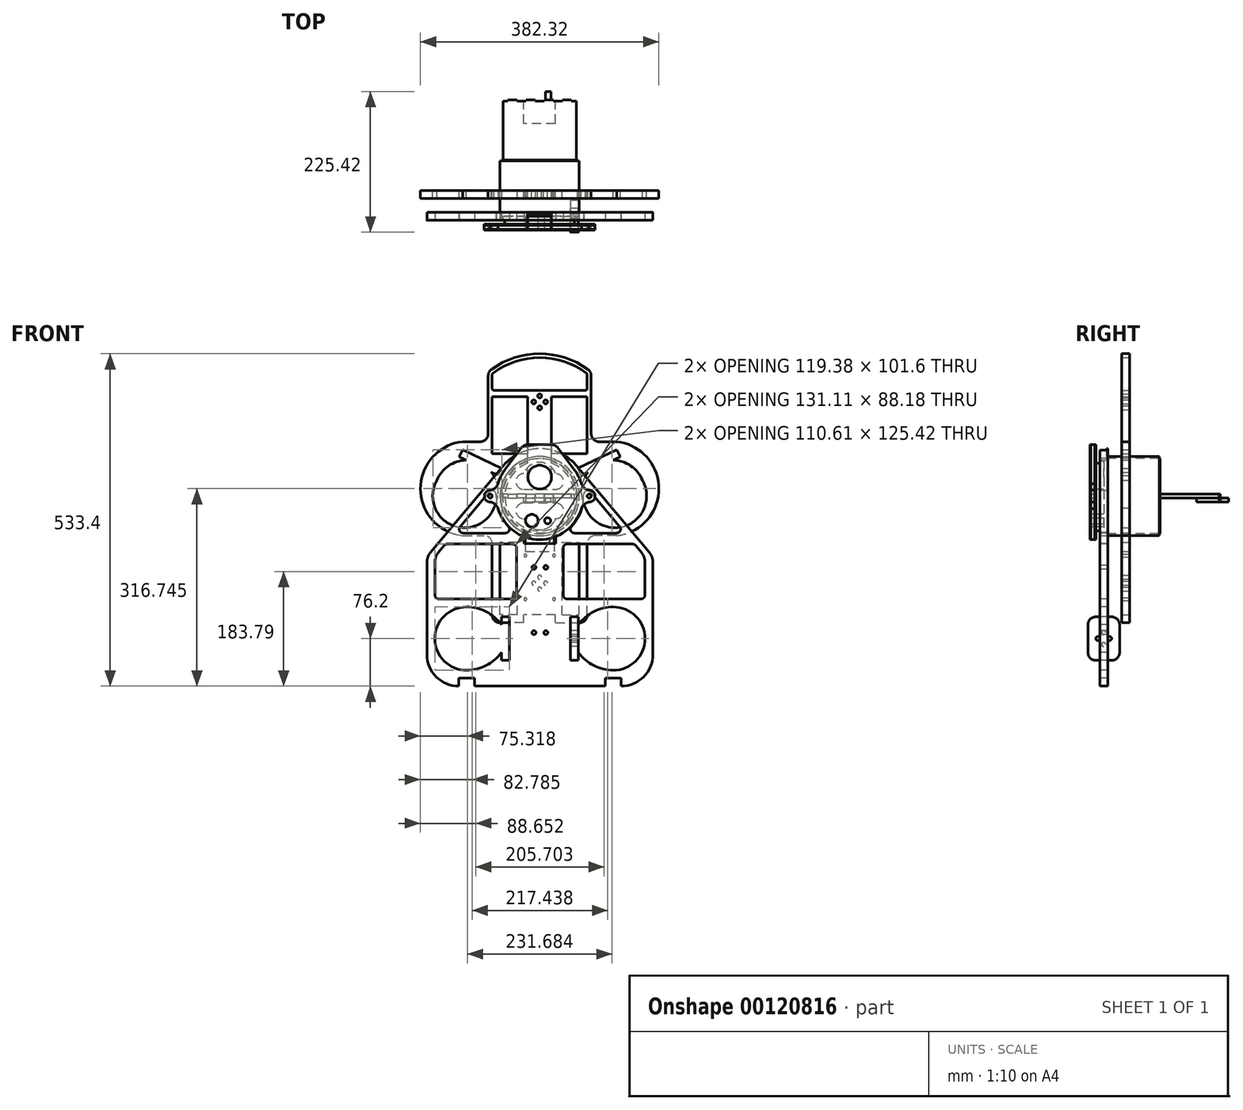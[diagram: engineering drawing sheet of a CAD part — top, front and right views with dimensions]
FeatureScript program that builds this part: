
annotation { "Feature Type Name" : "Feature", "Feature Type Description" : "" }
export const myFeature = defineFeature(function(context is Context, id is Id, definition is map)
    precondition{}
    {
        {
            var Q0;
            Q0=qCreatedBy(makeId("Front.planeOp"),FACE);
            var sketch = newSketch(context, id + "F32", { "sketchPlane" : qUnion([Q0])});
            skCircle(sketch, "E0", {"center": v(0, 0) * mm, "radius": 63.5 * mm});
            skSolve(sketch);
        }
        {
            var Q0;
            Q0=makeQuery(id+"F32.imprint","IMPRINT",FACE,{"disambiguationData":[TD([[makeQuery(id+"F32.imprint","IMPRINT",EDGE,{"derivedFrom":sQuery(id+"F32.wireOp",EDGE,"E0")}),1.0]])]});
            extrude(context, id + "F0", {"entities" : qUnion([Q0]), "endBound" : BoundingType.SYMMETRIC, "depth" : 95.25 * mm});
        }
        {
            var Q0;
            Q0=makeQuery(id+"F0.opExtrude","CAP_FACE",FACE,{"disambiguationData":[OSD([sQuery(id+"F32.wireOp",EDGE,"E0")])],"isStart":false});
            var sketch = newSketch(context, id + "F1", { "sketchPlane" : qUnion([Q0])});
            skPoint(sketch, "E1.middle", {"position": v(0.34, 103.4) * mm});
            skLineSegment(sketch, "E2.right", {"start": v(-180.77, -106.35) * mm, "end": v(-180.77, -254) * mm});
            skLineSegment(sketch, "E3", {"start": v(-174.82, -90.02) * mm, "end": v(-58.18, 48.86) * mm});
            skLineSegment(sketch, "E4", {"start": v(-129.97, -304.8) * mm, "end": v(-129.97, -304.8) * mm});
            skLineSegment(sketch, "E5", {"start": v(0.34, 103.4) * mm, "end": v(0.34, -422.75) * mm, "construction": true});
            skLineSegment(sketch, "E6", {"start": v(-117.27, -177.8) * mm, "end": v(0, -177.8) * mm, "construction": true});
            skLineSegment(sketch, "E7", {"start": v(-117.27, -279.4) * mm, "end": v(0, -279.4) * mm, "construction": true});
            skLineSegment(sketch, "E8.top", {"start": v(-129.97, -292.1) * mm, "end": v(-104.57, -292.1) * mm});
            skLineSegment(sketch, "E8.left", {"start": v(-129.97, -304.8) * mm, "end": v(-129.97, -292.1) * mm});
            skLineSegment(sketch, "E8.right", {"start": v(-104.57, -304.8) * mm, "end": v(-104.57, -292.1) * mm});
            skPoint(sketch, "E8.middle", {"position": v(-117.27, -298.45) * mm});
            skLineSegment(sketch, "E9.trimOffspring", {"start": v(-104.57, -304.8) * mm, "end": v(0.34, -304.8) * mm});
            skLineSegment(sketch, "E10.bottom", {"start": v(0.34, -63.5) * mm, "end": v(0, -63.5) * mm});
            skLineSegment(sketch, "E10.top", {"start": v(25.74, -76.2) * mm, "end": v(-25.06, -76.2) * mm});
            skLineSegment(sketch, "E10.left", {"start": v(25.74, -58.05) * mm, "end": v(25.74, -76.2) * mm});
            skLineSegment(sketch, "E10.right", {"start": v(-25.06, -58.35) * mm, "end": v(-25.06, -76.2) * mm});
            skPoint(sketch, "E10.middle", {"position": v(0.34, -69.85) * mm});
            skArc(sketch, "E11.0", {"start": v(0, -63.5) * mm, "mid": v(0.17, -63.5) * mm, "end": v(0.34, -63.5) * mm});
            skArc(sketch, "E12", {"start": v(-33.6, -53.89) * mm, "mid": v(52.5, 35.7) * mm, "end": v(-62.46, -11.43) * mm});
            skArc(sketch, "E13.trimOffspring", {"start": v(25.74, -58.05) * mm, "mid": v(29.67, 56.14) * mm, "end": v(-62.46, -11.43) * mm});
            skPoint(sketch, "E14.orphan", {"position": v(25.74, -63.5) * mm});
            skPoint(sketch, "E15.orphan", {"position": v(-25.06, -63.5) * mm});
            skCircle(sketch, "E16", {"center": v(-9.18, -114.35) * mm, "radius": 3.18 * mm});
            skCircle(sketch, "E17.MirrorC", {"center": v(9.87, -114.35) * mm, "radius": 3.18 * mm});
            skCircle(sketch, "E18", {"center": v(-9.18, -219.08) * mm, "radius": 3.18 * mm});
            skCircle(sketch, "E19.MirrorC", {"center": v(9.87, -219.08) * mm, "radius": 3.18 * mm});
            skLineSegment(sketch, "E20.bottom", {"start": v(-48.69, -206.38) * mm, "end": v(-61.39, -206.38) * mm, "construction": true});
            skLineSegment(sketch, "E20.top", {"start": v(-48.69, -250.83) * mm, "end": v(-61.39, -250.83) * mm, "construction": true});
            skLineSegment(sketch, "E20.left", {"start": v(-48.69, -206.38) * mm, "end": v(-48.69, -250.83) * mm});
            skLineSegment(sketch, "E20.right", {"start": v(-61.39, -206.38) * mm, "end": v(-61.39, -250.83) * mm, "construction": true});
            skPoint(sketch, "E20.middle", {"position": v(-55.04, -228.6) * mm});
            skLineSegment(sketch, "E21.MirrorCS", {"start": v(49.37, -206.38) * mm, "end": v(49.37, -250.83) * mm});
            skLineSegment(sketch, "E22.MirrorCS", {"start": v(62.07, -206.38) * mm, "end": v(62.07, -250.83) * mm, "construction": true});
            skLineSegment(sketch, "E23", {"start": v(-61.39, -206.38) * mm, "end": v(-61.39, -193.67) * mm});
            skLineSegment(sketch, "E24", {"start": v(-61.39, -193.68) * mm, "end": v(-48.69, -193.68) * mm});
            skLineSegment(sketch, "E25", {"start": v(-48.69, -193.67) * mm, "end": v(-48.69, -206.38) * mm});
            skLineSegment(sketch, "E26", {"start": v(-117.27, -228.6) * mm, "end": v(-55.04, -228.6) * mm, "construction": true});
            skLineSegment(sketch, "E27.MirrorCS", {"start": v(-48.69, -263.53) * mm, "end": v(-48.69, -250.83) * mm});
            skLineSegment(sketch, "E28.MirrorCS", {"start": v(-61.39, -250.83) * mm, "end": v(-61.39, -263.53) * mm});
            skLineSegment(sketch, "E29.MirrorCS", {"start": v(-61.39, -263.53) * mm, "end": v(-48.69, -263.53) * mm});
            skLineSegment(sketch, "E30.MirrorCS", {"start": v(62.07, -206.38) * mm, "end": v(62.07, -193.67) * mm});
            skLineSegment(sketch, "E31.MirrorCS", {"start": v(62.07, -193.68) * mm, "end": v(49.37, -193.68) * mm});
            skLineSegment(sketch, "E32.MirrorCS", {"start": v(49.37, -193.67) * mm, "end": v(49.37, -206.38) * mm});
            skLineSegment(sketch, "E33.MirrorCS", {"start": v(62.07, -250.83) * mm, "end": v(62.07, -263.53) * mm});
            skLineSegment(sketch, "E34.MirrorCS", {"start": v(62.07, -263.53) * mm, "end": v(49.37, -263.53) * mm});
            skLineSegment(sketch, "E35.MirrorCS", {"start": v(49.37, -263.53) * mm, "end": v(49.37, -250.83) * mm});
            skPoint(sketch, "E36.MirrorCS.end.orphan", {"position": v(62.07, -206.38) * mm});
            skPoint(sketch, "E36.MirrorCS.start.orphan", {"position": v(49.37, -206.38) * mm});
            skPoint(sketch, "E37.MirrorCS.end.orphan", {"position": v(62.07, -250.83) * mm});
            skPoint(sketch, "E37.MirrorCS.start.orphan", {"position": v(49.37, -250.83) * mm});
            skLineSegment(sketch, "E38.MirrorCS", {"start": v(105.25, -304.8) * mm, "end": v(0.34, -304.8) * mm});
            skLineSegment(sketch, "E39.MirrorCS", {"start": v(105.25, -304.8) * mm, "end": v(105.25, -292.1) * mm});
            skLineSegment(sketch, "E40.MirrorCS", {"start": v(130.65, -292.1) * mm, "end": v(105.25, -292.1) * mm});
            skLineSegment(sketch, "E41.MirrorCS", {"start": v(130.65, -304.8) * mm, "end": v(130.65, -292.1) * mm});
            skLineSegment(sketch, "E42.MirrorCS", {"start": v(181.45, -97.1) * mm, "end": v(181.45, -254) * mm});
            skLineSegment(sketch, "E43.MirrorCS", {"start": v(181.45, -97.1) * mm, "end": v(58.86, 48.86) * mm});
            skArc(sketch, "E44", {"start": v(58.86, 48.86) * mm, "mid": v(0.34, 76.13) * mm, "end": v(-58.18, 48.86) * mm});
            skPoint(sketch, "E45.visualSharp", {"position": v(-180.77, -304.8) * mm});
            skArc(sketch, "E45.filletArc", {"start": v(-180.77, -254) * mm, "mid": v(-165.89, -289.92) * mm, "end": v(-129.97, -304.8) * mm});
            skArc(sketch, "E46.MirrorCS", {"start": v(181.45, -254) * mm, "mid": v(166.57, -289.92) * mm, "end": v(130.65, -304.8) * mm});
            skPoint(sketch, "E47.MirrorCS.end.orphan", {"position": v(130.65, -304.8) * mm});
            skLineSegment(sketch, "E48", {"start": v(-168.07, -158.75) * mm, "end": v(-168.07, -106.35) * mm});
            skLineSegment(sketch, "E49", {"start": v(-162.12, -90.02) * mm, "end": v(-153.02, -79.19) * mm});
            skArc(sketch, "E50", {"start": v(-62.46, -11.43) * mm, "mid": v(-52.5, -35.7) * mm, "end": v(-33.6, -53.89) * mm});
            skArc(sketch, "E51", {"start": v(-33.6, -53.89) * mm, "mid": v(-29.4, -56.28) * mm, "end": v(-25.06, -58.35) * mm});
            skLineSegment(sketch, "E52", {"start": v(-62.46, -11.43) * mm, "end": v(-62.46, -11.43) * mm});
            skLineSegment(sketch, "E53", {"start": v(-33.6, -53.89) * mm, "end": v(-33.6, -53.89) * mm});
            skArc(sketch, "E54.0", {"start": v(-69.81, 2.25) * mm, "mid": v(-65.18, -25.12) * mm, "end": v(-50.25, -48.52) * mm});
            skLineSegment(sketch, "E55", {"start": v(-36.95, -83.27) * mm, "end": v(-36.95, -158.75) * mm});
            skLineSegment(sketch, "E56", {"start": v(-64.97, 25.65) * mm, "end": v(-64.97, 25.65) * mm});
            skPoint(sketch, "E57.visualSharp", {"position": v(-180.77, -97.1) * mm});
            skArc(sketch, "E57.filletArc", {"start": v(-174.82, -90.02) * mm, "mid": v(-179.23, -97.66) * mm, "end": v(-180.77, -106.35) * mm});
            skPoint(sketch, "E58.visualSharp", {"position": v(-168.07, -97.1) * mm});
            skArc(sketch, "E58.filletArc", {"start": v(-162.12, -90.02) * mm, "mid": v(-166.53, -97.66) * mm, "end": v(-168.07, -106.35) * mm});
            skArc(sketch, "E59.MirrorCS", {"start": v(162.8, -90.02) * mm, "mid": v(167.22, -97.66) * mm, "end": v(168.75, -106.35) * mm});
            skArc(sketch, "E60.MirrorCS", {"start": v(175.5, -90.02) * mm, "mid": v(179.92, -97.66) * mm, "end": v(181.45, -106.35) * mm});
            skLineSegment(sketch, "E61.MirrorCS", {"start": v(128.22, -48.84) * mm, "end": v(81.71, 6.54) * mm});
            skArc(sketch, "E62.MirrorCS", {"start": v(70.5, 2.25) * mm, "mid": v(65.87, -25.12) * mm, "end": v(50.94, -48.52) * mm});
            skLineSegment(sketch, "E63.MirrorCS", {"start": v(37.64, -59.28) * mm, "end": v(37.64, -76.92) * mm, "construction": true});
            skLineSegment(sketch, "E64.MirrorCS", {"start": v(168.75, -158.75) * mm, "end": v(168.75, -106.35) * mm});
            skLineSegment(sketch, "E65", {"start": v(74.77, -201.84) * mm, "end": v(74.77, -201.84) * mm});
            skLineSegment(sketch, "E66.bottom", {"start": v(-54.82, -59.28) * mm, "end": v(-122.67, -59.28) * mm});
            skLineSegment(sketch, "E66.top", {"start": v(-43.3, -76.92) * mm, "end": v(-148.16, -76.92) * mm});
            skLineSegment(sketch, "E66.left", {"start": v(-36.95, -59.28) * mm, "end": v(-36.95, -76.92) * mm, "construction": true});
            skLineSegment(sketch, "E67.MirrorCS", {"start": v(43.99, -76.92) * mm, "end": v(148.84, -76.92) * mm});
            skLineSegment(sketch, "E68.MirrorCS", {"start": v(55.5, -59.28) * mm, "end": v(123.36, -59.28) * mm});
            skArc(sketch, "E69.MirrorCS", {"start": v(117.95, -279.4) * mm, "mid": v(86.57, -271.84) * mm, "end": v(62.07, -250.83) * mm});
            skArc(sketch, "E70.MirrorCS", {"start": v(168.75, -228.6) * mm, "mid": v(153.87, -264.52) * mm, "end": v(117.95, -279.4) * mm});
            skArc(sketch, "E71", {"start": v(-117.27, -279.4) * mm, "mid": v(-85.88, -271.84) * mm, "end": v(-61.39, -250.83) * mm});
            skArc(sketch, "E72", {"start": v(-168.07, -228.6) * mm, "mid": v(-153.19, -264.52) * mm, "end": v(-117.27, -279.4) * mm});
            skArc(sketch, "E73.MirrorCS", {"start": v(-117.27, -177.8) * mm, "mid": v(-85.88, -185.36) * mm, "end": v(-61.39, -206.38) * mm});
            skArc(sketch, "E74.MirrorCS", {"start": v(-168.07, -228.6) * mm, "mid": v(-153.19, -192.68) * mm, "end": v(-117.27, -177.8) * mm});
            skLineSegment(sketch, "E75", {"start": v(-43.3, -165.1) * mm, "end": v(-161.72, -165.1) * mm});
            skArc(sketch, "E76.MirrorCS", {"start": v(117.95, -177.8) * mm, "mid": v(86.57, -185.36) * mm, "end": v(62.07, -206.38) * mm});
            skArc(sketch, "E77.MirrorCS", {"start": v(168.75, -228.6) * mm, "mid": v(153.87, -192.68) * mm, "end": v(117.95, -177.8) * mm});
            skLineSegment(sketch, "E78.MirrorCS", {"start": v(43.99, -165.1) * mm, "end": v(162.4, -165.1) * mm});
            skLineSegment(sketch, "E79", {"start": v(37.64, -83.27) * mm, "end": v(37.64, -158.75) * mm});
            skLineSegment(sketch, "E80", {"start": v(-36.95, -76.92) * mm, "end": v(-36.95, -76.92) * mm});
            skPoint(sketch, "E81.visualSharp", {"position": v(-36.95, -165.1) * mm});
            skArc(sketch, "E81.filletArc", {"start": v(-43.3, -165.1) * mm, "mid": v(-38.81, -163.24) * mm, "end": v(-36.95, -158.75) * mm});
            skPoint(sketch, "E82.newPointA", {"position": v(-168.07, -165.1) * mm});
            skPoint(sketch, "E82.newPointB", {"position": v(-168.07, -163.76) * mm});
            skArc(sketch, "E82.filletArc", {"start": v(-168.07, -158.75) * mm, "mid": v(-166.2, -163.24) * mm, "end": v(-161.72, -165.1) * mm});
            skPoint(sketch, "E83.newPointA", {"position": v(-36.95, -59.28) * mm});
            skPoint(sketch, "E83.newPointB", {"position": v(-36.95, -76.92) * mm});
            skArc(sketch, "E83.filletArc", {"start": v(-36.95, -83.27) * mm, "mid": v(-38.81, -78.78) * mm, "end": v(-43.3, -76.92) * mm});
            skPoint(sketch, "E84.visualSharp", {"position": v(37.64, -76.92) * mm});
            skArc(sketch, "E84.filletArc", {"start": v(43.99, -76.92) * mm, "mid": v(39.5, -78.78) * mm, "end": v(37.64, -83.27) * mm});
            skPoint(sketch, "E85.newPointA", {"position": v(-64.97, 25.65) * mm});
            skPoint(sketch, "E85.newPointB", {"position": v(-151.11, -76.92) * mm});
            skArc(sketch, "E85.filletArc", {"start": v(-148.16, -76.92) * mm, "mid": v(-150.84, -77.51) * mm, "end": v(-153.02, -79.19) * mm});
            skLineSegment(sketch, "E86", {"start": v(-81.02, 6.54) * mm, "end": v(-127.53, -48.84) * mm});
            skPoint(sketch, "E87.visualSharp", {"position": v(-136.3, -59.28) * mm});
            skArc(sketch, "E87.filletArc", {"start": v(-127.53, -48.84) * mm, "mid": v(-128.43, -55.6) * mm, "end": v(-122.67, -59.28) * mm});
            skArc(sketch, "E88.filletArc", {"start": v(-69.81, 2.25) * mm, "mid": v(-73.9, 8.38) * mm, "end": v(-81.02, 6.54) * mm});
            skArc(sketch, "E89.filletArc", {"start": v(-54.82, -59.28) * mm, "mid": v(-48.97, -55.4) * mm, "end": v(-50.25, -48.52) * mm});
            skPoint(sketch, "E90.visualSharp", {"position": v(37.64, -59.28) * mm});
            skArc(sketch, "E90.filletArc", {"start": v(50.94, -48.52) * mm, "mid": v(49.66, -55.4) * mm, "end": v(55.5, -59.28) * mm});
            skPoint(sketch, "E91.visualSharp", {"position": v(65.66, 25.65) * mm});
            skArc(sketch, "E91.filletArc", {"start": v(81.71, 6.54) * mm, "mid": v(74.58, 8.38) * mm, "end": v(70.5, 2.25) * mm});
            skPoint(sketch, "E92.newPointA", {"position": v(162.8, -90.02) * mm});
            skPoint(sketch, "E92.newPointB", {"position": v(136.98, -59.28) * mm});
            skArc(sketch, "E92.filletArc", {"start": v(123.36, -59.28) * mm, "mid": v(129.11, -55.6) * mm, "end": v(128.22, -48.84) * mm});
            skLineSegment(sketch, "E93", {"start": v(162.8, -90.02) * mm, "end": v(153.7, -79.19) * mm});
            skPoint(sketch, "E94.visualSharp", {"position": v(151.8, -76.92) * mm});
            skArc(sketch, "E94.filletArc", {"start": v(153.7, -79.19) * mm, "mid": v(151.53, -77.51) * mm, "end": v(148.84, -76.92) * mm});
            skPoint(sketch, "E95.newPointA", {"position": v(168.75, -163.76) * mm});
            skPoint(sketch, "E95.newPointB", {"position": v(168.75, -165.1) * mm});
            skArc(sketch, "E95.filletArc", {"start": v(162.4, -165.1) * mm, "mid": v(166.9, -163.24) * mm, "end": v(168.75, -158.75) * mm});
            skPoint(sketch, "E96.visualSharp", {"position": v(37.64, -165.1) * mm});
            skArc(sketch, "E96.filletArc", {"start": v(37.64, -158.75) * mm, "mid": v(39.5, -163.24) * mm, "end": v(43.99, -165.1) * mm});
            skSolve(sketch);
        }
        {
            var Q0;
            Q0=makeQuery(id+"F1.imprint","IMPRINT",FACE,{"disambiguationData":[TD([[makeQuery(id+"F1.imprint","IMPRINT",EDGE,{"derivedFrom":sQuery(id+"F1.wireOp",EDGE,"E2.left")}),-1.0]])]});
            var Q1;
            Q1=makeQuery(id+"F1.imprint","IMPRINT",FACE,{"disambiguationData":[TD([[makeQuery(id+"F1.imprint","IMPRINT",EDGE,{"derivedFrom":makeQuery(id+"F0.opExtrude","CAP_EDGE",EDGE,{"disambiguationData":[OSD([sQuery(id+"F32.wireOp",EDGE,"E0")])],"isStart":false})}),-1.0]])]});
            var Q2;
            {var subQ0=sQuery(id+"F1.wireOp",EDGE,"E10.left");Q2=makeQuery(id+"F1.imprint","IMPRINT",FACE,{"disambiguationData":[TD([[makeQuery(id+"F1.imprint","IMPRINT",EDGE,{"derivedFrom":subQ0}),1.0]])]});}
            var Q3;
            Q3=makeQuery(id+"F1.imprint","IMPRINT",FACE,{"disambiguationData":[TD([[makeQuery(id+"F1.imprint","IMPRINT",EDGE,{"derivedFrom":sQuery(id+"F1.wireOp",EDGE,"E2.right")}),1.0]])]});
            var Q4;
            {var subQ0=sQuery(id+"F1.wireOp",EDGE,"E66.bottom");Q4=makeQuery(id+"F1.imprint","IMPRINT",FACE,{"disambiguationData":[TD([[makeQuery(id+"F1.imprint","IMPRINT",EDGE,{"derivedFrom":subQ0}),1.0]])]});}
            var Q5;
            {var subQ0=sQuery(id+"F1.wireOp",EDGE,"E67.MirrorCS");Q5=makeQuery(id+"F1.imprint","IMPRINT",FACE,{"disambiguationData":[TD([[makeQuery(id+"F1.imprint","IMPRINT",EDGE,{"derivedFrom":subQ0}),1.0]])]});}
            extrude(context, id + "F2", {"entities" : qUnion([Q0, Q1, Q2, Q3, Q4, Q5]), "oppositeDirection" : true, "depth" : 12.7 * mm});
        }
        {
            var Q0;
            Q0=makeQuery(id+"F0.opExtrude","CAP_FACE",FACE,{"disambiguationData":[OSD([sQuery(id+"F32.wireOp",EDGE,"E0")])],"isStart":false});
            var sketch = newSketch(context, id + "F3", { "sketchPlane" : qUnion([Q0])});
            skCircle(sketch, "E97", {"center": v(0, 0) * mm, "radius": 60.2 * mm});
            skSolve(sketch);
        }
        {
            var Q0;
            Q0=makeQuery(id+"F3.imprint","IMPRINT",FACE,{"disambiguationData":[TD([[makeQuery(id+"F3.imprint","IMPRINT",EDGE,{"derivedFrom":sQuery(id+"F3.wireOp",EDGE,"E97")}),1.0]])]});
            extrude(context, id + "F4", {"entities" : qUnion([Q0]), "operationType" : NewBodyOperationType.REMOVE, "endBound" : BoundingType.THROUGH_ALL, "oppositeDirection" : true, "depth" : 25.4 * mm});
        }
        {
            var Q0;
            Q0=makeQuery(id+"F0.opExtrude","CAP_FACE",FACE,{"disambiguationData":[OSD([sQuery(id+"F32.wireOp",EDGE,"E0")])],"isStart":false});
            var sketch = newSketch(context, id + "F5", { "sketchPlane" : qUnion([Q0])});
            skCircle(sketch, "E98", {"center": v(0, 0) * mm, "radius": 59.2 * mm});
            skSolve(sketch);
        }
        {
            var Q0;
            Q0=makeQuery(id+"F5.imprint","IMPRINT",FACE,{"disambiguationData":[TD([[makeQuery(id+"F5.imprint","IMPRINT",EDGE,{"derivedFrom":sQuery(id+"F5.wireOp",EDGE,"E98")}),1.0]])]});
            extrude(context, id + "F6", {"entities" : qUnion([Q0]), "oppositeDirection" : true, "depth" : 6.35 * mm});
        }
        {
            var Q0;
            Q0=makeQuery(id+"F6.opExtrude","CAP_FACE",FACE,{"disambiguationData":[OSD([sQuery(id+"F5.wireOp",EDGE,"E98")])],"isStart":true});
            var sketch = newSketch(context, id + "F7", { "sketchPlane" : qUnion([Q0])});
            skCircle(sketch, "E99", {"center": v(0, 0) * mm, "radius": 55.88 * mm});
            skSolve(sketch);
        }
        {
            var Q0;
            Q0 = qSketchRegion(id + "F7", true);
            extrude(context, id + "F8", {"entities" : qUnion([Q0]), "depth" : 6.35 * mm});
        }
        {
            var Q0;
            Q0=makeQuery(id+"F8.opExtrude","CAP_FACE",FACE,{"disambiguationData":[OSD([sQuery(id+"F7.wireOp",EDGE,"E99")])],"isStart":false});
            var sketch = newSketch(context, id + "F9", { "sketchPlane" : qUnion([Q0])});
            skArc(sketch, "E100", {"start": v(66.89, 20) * mm, "mid": v(0, 69.81) * mm, "end": v(-66.89, 20) * mm});
            skCircle(sketch, "E101", {"center": v(-79.34, 0) * mm, "radius": 3.18 * mm});
            skArc(sketch, "E102.0", {"start": v(-79.34, 9.52) * mm, "mid": v(-88.86, 0) * mm, "end": v(-79.34, -9.52) * mm});
            skLineSegment(sketch, "E103", {"start": v(-79.4, 9.53) * mm, "end": v(-79.34, 9.53) * mm});
            skArc(sketch, "E104", {"start": v(-79.34, 9.53) * mm, "mid": v(-71.62, 13) * mm, "end": v(-66.89, 20) * mm});
            skArc(sketch, "E105.MirrorCS", {"start": v(-79.34, -9.53) * mm, "mid": v(-71.62, -13) * mm, "end": v(-66.89, -20) * mm});
            skArc(sketch, "E106.MirrorCS", {"start": v(79.34, 9.53) * mm, "mid": v(71.62, 13) * mm, "end": v(66.89, 20) * mm});
            skArc(sketch, "E107.MirrorCS", {"start": v(79.34, 9.52) * mm, "mid": v(88.86, 0) * mm, "end": v(79.34, -9.52) * mm});
            skArc(sketch, "E108.MirrorCS", {"start": v(79.34, -9.53) * mm, "mid": v(71.62, -13) * mm, "end": v(66.89, -20) * mm});
            skCircle(sketch, "E109.MirrorC", {"center": v(79.34, 0) * mm, "radius": 3.18 * mm});
            skArc(sketch, "E110.trimOffspring", {"start": v(-66.89, -20) * mm, "mid": v(0, -69.81) * mm, "end": v(66.89, -20) * mm});
            skLineSegment(sketch, "E111", {"start": v(0, 69.81) * mm, "end": v(0, 82.51) * mm, "construction": true});
            skLineSegment(sketch, "E112", {"start": v(-19.05, 82.51) * mm, "end": v(19.05, 82.51) * mm});
            skLineSegment(sketch, "E113", {"start": v(-29.21, 77.43) * mm, "end": v(-55.86, 41.87) * mm});
            skLineSegment(sketch, "E114", {"start": v(29.21, 77.43) * mm, "end": v(55.86, 41.87) * mm});
            skPoint(sketch, "E115.visualSharp", {"position": v(-25.4, 82.51) * mm});
            skArc(sketch, "E115.filletArc", {"start": v(-19.05, 82.51) * mm, "mid": v(-24.73, 81.17) * mm, "end": v(-29.21, 77.43) * mm});
            skPoint(sketch, "E116.visualSharp", {"position": v(25.4, 82.51) * mm});
            skArc(sketch, "E116.filletArc", {"start": v(29.21, 77.43) * mm, "mid": v(24.73, 81.17) * mm, "end": v(19.05, 82.51) * mm});
            skSolve(sketch);
        }
        {
            var Q0;
            Q0 = qSketchRegion(id + "F9", true);
            extrude(context, id + "F10", {"entities" : qUnion([Q0]), "depth" : 1.59 * mm});
        }
        {
            var Q0;
            Q0=makeQuery(id+"F10.opExtrude","CAP_FACE",FACE,{"disambiguationData":[OSD([sQuery(id+"F9.wireOp",EDGE,"E100")])],"isStart":false});
            extrude(context, id + "F11", {"entities" : qUnion([Q0]), "depth" : 6.35 * mm});
        }
        {
            var Q0;
            Q0=makeQuery(id+"F11.opExtrude","CAP_FACE",FACE,{"disambiguationData":[OSD([sQuery(id+"F9.wireOp",EDGE,"E100")])],"isStart":false});
            extrude(context, id + "F12", {"entities" : qUnion([Q0]), "depth" : 1.59 * mm});
        }
        {
            var Q0;
            Q0=makeQuery(id+"F6.opExtrude","CAP_FACE",FACE,{"disambiguationData":[OSD([sQuery(id+"F5.wireOp",EDGE,"E98")])],"isStart":false});
            var sketch = newSketch(context, id + "F13", { "sketchPlane" : qUnion([Q0])});
            skCircle(sketch, "E117", {"center": v(12.7, -39.5) * mm, "radius": 5 * mm});
            skCircle(sketch, "E118.MirrorC", {"center": v(-12.7, -39.5) * mm, "radius": 5 * mm});
            skSolve(sketch);
        }
        {
            var Q0;
            Q0 = qSketchRegion(id + "F13", true);
            extrude(context, id + "F14", {"entities" : qUnion([Q0]), "operationType" : NewBodyOperationType.REMOVE, "endBound" : BoundingType.THROUGH_ALL, "oppositeDirection" : true, "depth" : 25.4 * mm});
        }
        {
            var Q0;
            Q0=makeQuery(id+"F6.opExtrude","CAP_FACE",FACE,{"disambiguationData":[OSD([sQuery(id+"F5.wireOp",EDGE,"E98")])],"isStart":false});
            var sketch = newSketch(context, id + "F15", { "sketchPlane" : qUnion([Q0])});
            skCircle(sketch, "E119", {"center": v(0, 30.48) * mm, "radius": 19.05 * mm});
            skCircle(sketch, "E120.0", {"center": v(0, 0) * mm, "radius": 55.88 * mm});
            skSolve(sketch);
        }
        {
            var Q0;
            Q0=makeQuery(id+"F15.imprint","IMPRINT",FACE,{"disambiguationData":[TD([[makeQuery(id+"F15.imprint","IMPRINT",EDGE,{"derivedFrom":sQuery(id+"F15.wireOp",EDGE,"E119")}),1.0]])]});
            extrude(context, id + "F16", {"entities" : qUnion([Q0]), "operationType" : NewBodyOperationType.REMOVE, "oppositeDirection" : true, "depth" : 25.4 * mm});
        }
        {
            var Q0;
            Q0=makeQuery(id+"F11.opExtrude","CAP_FACE",FACE,{"disambiguationData":[OSD([sQuery(id+"F9.wireOp",EDGE,"E100"),sQuery(id+"F9.wireOp",EDGE,"E101"),sQuery(id+"F9.wireOp",EDGE,"E102.0"),sQuery(id+"F9.wireOp",EDGE,"E104"),sQuery(id+"F9.wireOp",EDGE,"E105.MirrorCS"),sQuery(id+"F9.wireOp",EDGE,"E106.MirrorCS"),sQuery(id+"F9.wireOp",EDGE,"E107.MirrorCS"),sQuery(id+"F9.wireOp",EDGE,"E108.MirrorCS"),sQuery(id+"F9.wireOp",EDGE,"E109.MirrorC")])],"isStart":false});
            var sketch = newSketch(context, id + "F17", { "sketchPlane" : qUnion([Q0])});
            skArc(sketch, "E121.0", {"start": v(-10.1, 14.33) * mm, "mid": v(0, 11.43) * mm, "end": v(10.1, 14.33) * mm});
            skLineSegment(sketch, "E122", {"start": v(-19.05, 30.48) * mm, "end": v(-19.05, 82.51) * mm});
            skLineSegment(sketch, "E123", {"start": v(19.05, 30.48) * mm, "end": v(19.05, 82.51) * mm});
            skArc(sketch, "E124.0", {"start": v(-19.05, 30.48) * mm, "mid": v(0, 11.43) * mm, "end": v(19.05, 30.48) * mm});
            skSolve(sketch);
        }
        {
            var Q0;
            {var subQ3=sQuery(id+"F17.wireOp",EDGE,"E122");Q0=makeQuery(id+"F17.imprint","IMPRINT",FACE,{"disambiguationData":[TD([[makeQuery(id+"F17.imprint","IMPRINT",EDGE,{"derivedFrom":subQ3}),-1.0]])]});}
            extrude(context, id + "F18", {"entities" : qUnion([Q0]), "operationType" : NewBodyOperationType.REMOVE, "oppositeDirection" : true, "depth" : 25.4 * mm});
        }
        {
            var Q0;
            Q0=makeQuery(id+"F12.opExtrude","CAP_FACE",FACE,{"disambiguationData":[OSD([sQuery(id+"F9.wireOp",EDGE,"E100"),sQuery(id+"F9.wireOp",EDGE,"E101"),sQuery(id+"F9.wireOp",EDGE,"E102.0"),sQuery(id+"F9.wireOp",EDGE,"E104"),sQuery(id+"F9.wireOp",EDGE,"E105.MirrorCS"),sQuery(id+"F9.wireOp",EDGE,"E106.MirrorCS"),sQuery(id+"F9.wireOp",EDGE,"E107.MirrorCS"),sQuery(id+"F9.wireOp",EDGE,"E108.MirrorCS"),sQuery(id+"F9.wireOp",EDGE,"E109.MirrorC"),sQuery(id+"F9.wireOp",EDGE,"E110.trimOffspring"),sQuery(id+"F9.wireOp",EDGE,"E112"),sQuery(id+"F9.wireOp",EDGE,"E113"),sQuery(id+"F9.wireOp",EDGE,"E114"),sQuery(id+"F9.wireOp",EDGE,"E115.filletArc"),sQuery(id+"F9.wireOp",EDGE,"E116.filletArc")])],"isStart":false});
            var sketch = newSketch(context, id + "F19", { "sketchPlane" : qUnion([Q0])});
            skCircle(sketch, "E125.0", {"center": v(-12.7, -39.5) * mm, "radius": 5 * mm});
            skCircle(sketch, "E126.0", {"center": v(12.7, -39.5) * mm, "radius": 5 * mm});
            skCircle(sketch, "E127", {"center": v(-12.7, -39.5) * mm, "radius": 10.16 * mm});
            skCircle(sketch, "E128.MirrorC", {"center": v(12.7, -39.5) * mm, "radius": 10.16 * mm});
            skSolve(sketch);
        }
        {
            var Q0;
            Q0=makeQuery(id+"F19.imprint","IMPRINT",FACE,{"disambiguationData":[TD([[makeQuery(id+"F19.imprint","IMPRINT",EDGE,{"derivedFrom":sQuery(id+"F19.wireOp",EDGE,"E125.0")}),-1.0]])]});
            var Q1;
            Q1=makeQuery(id+"F19.imprint","IMPRINT",FACE,{"disambiguationData":[TD([[makeQuery(id+"F19.imprint","IMPRINT",EDGE,{"derivedFrom":sQuery(id+"F19.wireOp",EDGE,"E126.0")}),1.0]])]});
            extrude(context, id + "F20", {"entities" : qUnion([Q0, Q1]), "operationType" : NewBodyOperationType.REMOVE, "endBound" : BoundingType.THROUGH_ALL, "oppositeDirection" : true, "depth" : 76.2 * mm});
        }
        {
            var Q0;
            Q0=makeQuery(id+"F0.opExtrude","CAP_FACE",FACE,{"disambiguationData":[OSD([sQuery(id+"F32.wireOp",EDGE,"E0")])],"isStart":true});
            var sketch = newSketch(context, id + "F21", { "sketchPlane" : qUnion([Q0])});
            skCircle(sketch, "E129.0", {"center": v(0, 0) * mm, "radius": 60.2 * mm});
            skLineSegment(sketch, "E130", {"start": v(-50.8, -2.86) * mm, "end": v(-50.8, 2.86) * mm});
            skLineSegment(sketch, "E131", {"start": v(-50.8, 2.86) * mm, "end": v(-36.29, 2.86) * mm});
            skLineSegment(sketch, "E132", {"start": v(50.8, 2.86) * mm, "end": v(50.8, -2.86) * mm});
            skLineSegment(sketch, "E133", {"start": v(-50.8, -2.86) * mm, "end": v(-36.29, -2.86) * mm});
            skLineSegment(sketch, "E134", {"start": v(-36.29, -2.86) * mm, "end": v(-36.29, 2.86) * mm});
            skLineSegment(sketch, "E135", {"start": v(-21.77, -2.86) * mm, "end": v(-21.77, 2.86) * mm});
            skLineSegment(sketch, "E136", {"start": v(-21.77, -2.86) * mm, "end": v(-7.26, -2.86) * mm});
            skLineSegment(sketch, "E137", {"start": v(-7.26, -2.86) * mm, "end": v(-7.26, 2.86) * mm});
            skLineSegment(sketch, "E138", {"start": v(50.8, -2.86) * mm, "end": v(36.29, -2.86) * mm});
            skLineSegment(sketch, "E139", {"start": v(36.29, -2.86) * mm, "end": v(36.29, 2.86) * mm});
            skLineSegment(sketch, "E140", {"start": v(21.77, -2.86) * mm, "end": v(21.77, 2.86) * mm});
            skLineSegment(sketch, "E141", {"start": v(21.77, -2.86) * mm, "end": v(7.26, -2.86) * mm});
            skLineSegment(sketch, "E142", {"start": v(7.26, -2.86) * mm, "end": v(7.26, 2.86) * mm});
            skPoint(sketch, "E143", {"position": v(-50.8, 0) * mm});
            skPoint(sketch, "E144", {"position": v(0, 2.86) * mm});
            skLineSegment(sketch, "E145.trimOffspring", {"start": v(-21.77, 2.86) * mm, "end": v(-7.26, 2.86) * mm});
            skLineSegment(sketch, "E146.trimOffspring", {"start": v(7.26, 2.86) * mm, "end": v(21.77, 2.86) * mm});
            skLineSegment(sketch, "E147.trimOffspring", {"start": v(36.29, 2.86) * mm, "end": v(50.8, 2.86) * mm});
            skLineSegment(sketch, "E148.bottom", {"start": v(25.4, 36.18) * mm, "end": v(-25.4, 36.18) * mm, "construction": true});
            skLineSegment(sketch, "E148.top", {"start": v(25.4, 10.78) * mm, "end": v(-25.4, 10.78) * mm});
            skPoint(sketch, "E148.middle", {"position": v(0, 23.48) * mm});
            skArc(sketch, "E149", {"start": v(-25.4, 36.18) * mm, "mid": v(-38.1, 23.48) * mm, "end": v(-25.4, 10.78) * mm});
            skArc(sketch, "E150", {"start": v(25.4, 10.78) * mm, "mid": v(38.1, 23.48) * mm, "end": v(25.4, 36.18) * mm});
            skLineSegment(sketch, "E151.MirrorCS", {"start": v(25.4, -10.78) * mm, "end": v(-25.4, -10.78) * mm});
            skArc(sketch, "E152.MirrorCS", {"start": v(25.4, -10.78) * mm, "mid": v(38.1, -23.48) * mm, "end": v(25.4, -36.18) * mm});
            skLineSegment(sketch, "E153.MirrorCS", {"start": v(25.4, -36.18) * mm, "end": v(-25.4, -36.18) * mm, "construction": true});
            skArc(sketch, "E154.MirrorCS", {"start": v(-25.4, -36.18) * mm, "mid": v(-38.1, -23.48) * mm, "end": v(-25.4, -10.78) * mm});
            skArc(sketch, "E155", {"start": v(25.4, 36.18) * mm, "mid": v(0, 54.13) * mm, "end": v(-25.4, 36.18) * mm});
            skLineSegment(sketch, "E156", {"start": v(50.8, 0) * mm, "end": v(-50.8, 0) * mm});
            skArc(sketch, "E157.MirrorCS", {"start": v(25.4, -36.18) * mm, "mid": v(0, -54.13) * mm, "end": v(-25.4, -36.18) * mm});
            skSolve(sketch);
        }
        {
            var Q0;
            Q0=makeQuery(id+"F21.imprint","IMPRINT",FACE,{"disambiguationData":[TD([[makeQuery(id+"F21.imprint","IMPRINT",EDGE,{"derivedFrom":sQuery(id+"F21.wireOp",EDGE,"E129.0")}),-1.0]])]});
            extrude(context, id + "F22", {"entities" : qUnion([Q0]), "depth" : 1.52 * mm});
        }
        {
            var Q0;
            Q0=makeQuery(id+"F22.opExtrude","SWEPT_FACE",FACE,{"disambiguationData":[OSD([sQuery(id+"F21.wireOp",EDGE,"E133")])]});
            var sketch = newSketch(context, id + "F23", { "sketchPlane" : qUnion([Q0])});
            skLineSegment(sketch, "E158.0", {"start": v(50.8, 47.63) * mm, "end": v(36.29, 47.63) * mm});
            skLineSegment(sketch, "E159.0", {"start": v(36.29, 49.15) * mm, "end": v(36.29, 47.63) * mm});
            skLineSegment(sketch, "E160.0", {"start": v(50.8, 49.15) * mm, "end": v(50.8, 47.63) * mm});
            skLineSegment(sketch, "E161.0", {"start": v(21.77, 49.15) * mm, "end": v(21.77, 47.63) * mm});
            skLineSegment(sketch, "E162.0", {"start": v(21.77, 47.63) * mm, "end": v(7.26, 47.63) * mm});
            skLineSegment(sketch, "E163.0", {"start": v(7.26, 49.15) * mm, "end": v(7.26, 47.63) * mm});
            skLineSegment(sketch, "E164.0", {"start": v(-7.26, 49.15) * mm, "end": v(-7.26, 47.63) * mm});
            skLineSegment(sketch, "E165.0", {"start": v(-21.77, 47.63) * mm, "end": v(-7.26, 47.63) * mm});
            skLineSegment(sketch, "E166.0", {"start": v(-21.77, 49.15) * mm, "end": v(-21.77, 47.63) * mm});
            skLineSegment(sketch, "E167.0", {"start": v(-50.8, 49.15) * mm, "end": v(-50.8, 47.63) * mm});
            skLineSegment(sketch, "E168.0", {"start": v(-36.29, 49.15) * mm, "end": v(-36.29, 47.63) * mm});
            skLineSegment(sketch, "E169.0", {"start": v(-50.8, 47.63) * mm, "end": v(-36.29, 47.63) * mm});
            skLineSegment(sketch, "E170", {"start": v(50.8, 49.15) * mm, "end": v(58.93, 49.15) * mm});
            skLineSegment(sketch, "E171", {"start": v(58.93, 49.15) * mm, "end": v(58.93, 143.9) * mm});
            skLineSegment(sketch, "E172", {"start": v(-50.8, 49.15) * mm, "end": v(-58.93, 49.15) * mm});
            skLineSegment(sketch, "E173", {"start": v(-58.93, 49.15) * mm, "end": v(-58.93, 143.9) * mm});
            skLineSegment(sketch, "E174", {"start": v(58.93, 96.52) * mm, "end": v(-58.93, 96.52) * mm, "construction": true});
            skLineSegment(sketch, "E175.MirrorCS", {"start": v(50.8, 143.9) * mm, "end": v(58.93, 143.9) * mm});
            skLineSegment(sketch, "E176.MirrorCS", {"start": v(50.8, 143.9) * mm, "end": v(50.8, 145.42) * mm});
            skLineSegment(sketch, "E177.MirrorCS", {"start": v(50.8, 145.42) * mm, "end": v(36.29, 145.42) * mm});
            skLineSegment(sketch, "E178.MirrorCS", {"start": v(36.29, 143.9) * mm, "end": v(36.29, 145.42) * mm});
            skLineSegment(sketch, "E179.MirrorCS", {"start": v(21.77, 143.9) * mm, "end": v(21.77, 145.42) * mm});
            skLineSegment(sketch, "E180.MirrorCS", {"start": v(21.77, 145.42) * mm, "end": v(7.26, 145.42) * mm});
            skLineSegment(sketch, "E181.MirrorCS", {"start": v(7.26, 143.9) * mm, "end": v(7.26, 145.42) * mm});
            skLineSegment(sketch, "E182.MirrorCS", {"start": v(-7.26, 143.9) * mm, "end": v(-7.26, 145.42) * mm});
            skLineSegment(sketch, "E183.MirrorCS", {"start": v(-21.77, 145.42) * mm, "end": v(-7.26, 145.42) * mm});
            skLineSegment(sketch, "E184.MirrorCS", {"start": v(-21.77, 143.9) * mm, "end": v(-21.77, 145.42) * mm});
            skLineSegment(sketch, "E185.MirrorCS", {"start": v(-36.29, 143.9) * mm, "end": v(-36.29, 145.42) * mm});
            skLineSegment(sketch, "E186.MirrorCS", {"start": v(-50.8, 145.42) * mm, "end": v(-36.29, 145.42) * mm});
            skLineSegment(sketch, "E187.MirrorCS", {"start": v(-50.8, 143.9) * mm, "end": v(-50.8, 145.42) * mm});
            skLineSegment(sketch, "E188.MirrorCS", {"start": v(-50.8, 143.9) * mm, "end": v(-58.93, 143.9) * mm});
            skLineSegment(sketch, "E189", {"start": v(36.29, 49.15) * mm, "end": v(21.77, 49.15) * mm});
            skLineSegment(sketch, "E190", {"start": v(7.26, 49.15) * mm, "end": v(-7.26, 49.15) * mm});
            skLineSegment(sketch, "E191", {"start": v(-21.77, 49.15) * mm, "end": v(-36.29, 49.15) * mm});
            skLineSegment(sketch, "E192.MirrorCS", {"start": v(36.29, 143.9) * mm, "end": v(21.77, 143.9) * mm});
            skLineSegment(sketch, "E193.MirrorCS", {"start": v(7.26, 143.9) * mm, "end": v(-7.26, 143.9) * mm});
            skLineSegment(sketch, "E194.MirrorCS", {"start": v(-21.77, 143.9) * mm, "end": v(-36.29, 143.9) * mm});
            skLineSegment(sketch, "E195.0", {"start": v(60.2, 47.63) * mm, "end": v(-60.2, 47.63) * mm, "construction": true});
            skSolve(sketch);
        }
        {
            var Q0;
            Q0=makeQuery(id+"F23.imprint","IMPRINT",FACE,{"disambiguationData":[TD([[makeQuery(id+"F23.imprint","IMPRINT",EDGE,{"derivedFrom":sQuery(id+"F23.wireOp",EDGE,"E161.0")}),-1.0]])]});
            var Q1;
            Q1=makeQuery(id+"F23.imprint","IMPRINT",FACE,{"disambiguationData":[TD([[makeQuery(id+"F23.imprint","IMPRINT",EDGE,{"derivedFrom":sQuery(id+"F23.wireOp",EDGE,"E158.0")}),-1.0]])]});
            extrude(context, id + "F24", {"entities" : qUnion([Q0, Q1]), "depth" : 6.35 * mm});
        }
        {
            var Q0;
            Q0=makeQuery(id+"F2.opExtrude","SWEPT_FACE",FACE,{"disambiguationData":[OSD([sQuery(id+"F1.wireOp",EDGE,"E32.MirrorCS"),sQuery(id+"F1.wireOp",EDGE,"E21.MirrorCS"),sQuery(id+"F1.wireOp",EDGE,"E35.MirrorCS")])]});
            var sketch = newSketch(context, id + "F25", { "sketchPlane" : qUnion([Q0])});
            skLineSegment(sketch, "E196.bottom", {"start": v(-28.57, -193.67) * mm, "end": v(-53.97, -193.67) * mm});
            skLineSegment(sketch, "E196.top", {"start": v(-28.57, -263.53) * mm, "end": v(-53.97, -263.53) * mm});
            skLineSegment(sketch, "E196.left", {"start": v(-15.87, -206.38) * mm, "end": v(-15.87, -250.83) * mm});
            skLineSegment(sketch, "E196.right", {"start": v(-66.67, -206.38) * mm, "end": v(-66.67, -250.83) * mm});
            skPoint(sketch, "E196.middle", {"position": v(-41.27, -228.6) * mm});
            skPoint(sketch, "E196.middle.positionSnap0", {"position": v(-41.27, -193.68) * mm});
            skPoint(sketch, "E196.middle.positionSnap1", {"position": v(-47.63, -228.6) * mm});
            skPoint(sketch, "E196.cornerSnap0", {"position": v(-41.28, -193.68) * mm});
            skPoint(sketch, "E196.centerSnap0", {"position": v(-41.27, -193.68) * mm});
            skPoint(sketch, "E196.centerSnap1", {"position": v(-47.63, -228.6) * mm});
            skCircle(sketch, "E197", {"center": v(-41.27, -219.08) * mm, "radius": 3.18 * mm});
            skCircle(sketch, "E198", {"center": v(-50.8, -228.6) * mm, "radius": 3.18 * mm});
            skLineSegment(sketch, "E199", {"start": v(-41.27, -219.08) * mm, "end": v(-41.27, -228.6) * mm, "construction": true});
            skLineSegment(sketch, "E200", {"start": v(-41.27, -228.6) * mm, "end": v(-50.8, -228.6) * mm, "construction": true});
            skCircle(sketch, "E201.MirrorC", {"center": v(-31.75, -228.6) * mm, "radius": 3.18 * mm});
            skCircle(sketch, "E202.MirrorC", {"center": v(-41.27, -238.13) * mm, "radius": 3.18 * mm});
            skPoint(sketch, "E203.visualSharp", {"position": v(-66.67, -193.67) * mm});
            skArc(sketch, "E203.filletArc", {"start": v(-53.97, -193.68) * mm, "mid": v(-62.96, -197.4) * mm, "end": v(-66.67, -206.38) * mm});
            skPoint(sketch, "E204.visualSharp", {"position": v(-15.87, -193.67) * mm});
            skArc(sketch, "E204.filletArc", {"start": v(-15.87, -206.38) * mm, "mid": v(-19.6, -197.4) * mm, "end": v(-28.57, -193.68) * mm});
            skPoint(sketch, "E205.visualSharp", {"position": v(-15.87, -263.53) * mm});
            skArc(sketch, "E205.filletArc", {"start": v(-28.57, -263.53) * mm, "mid": v(-19.6, -259.8) * mm, "end": v(-15.88, -250.83) * mm});
            skPoint(sketch, "E206.visualSharp", {"position": v(-66.67, -263.53) * mm});
            skArc(sketch, "E206.filletArc", {"start": v(-66.67, -250.83) * mm, "mid": v(-62.96, -259.8) * mm, "end": v(-53.97, -263.53) * mm});
            skSolve(sketch);
        }
        {
            var Q0;
            {var subQ1=sQuery(id+"F25.wireOp",EDGE,"E196.right");Q0=makeQuery(id+"F25.imprint","IMPRINT",FACE,{"disambiguationData":[TD([[makeQuery(id+"F25.imprint","IMPRINT",EDGE,{"derivedFrom":subQ1}),1.0]])]});}
            var Q1;
            Q1=makeQuery(id+"F25.imprint","IMPRINT",FACE,{"disambiguationData":[TD([[makeQuery(id+"F25.imprint","IMPRINT",EDGE,{"derivedFrom":sQuery(id+"F25.wireOp",EDGE,"E197")}),-1.0]])]});
            var Q2;
            {var subQ1=sQuery(id+"F25.wireOp",EDGE,"E196.left");Q2=makeQuery(id+"F25.imprint","IMPRINT",FACE,{"disambiguationData":[TD([[makeQuery(id+"F25.imprint","IMPRINT",EDGE,{"derivedFrom":subQ1}),-1.0]])]});}
            extrude(context, id + "F26", {"entities" : qUnion([Q0, Q1, Q2]), "depth" : 12.7 * mm});
        }
        {
            var Q0;
            Q0=makeQuery(id+"F24.opExtrude","CAP_FACE",FACE,{"disambiguationData":[OSD([sQuery(id+"F23.wireOp",EDGE,"E158.0"),sQuery(id+"F23.wireOp",EDGE,"E159.0"),sQuery(id+"F23.wireOp",EDGE,"E160.0"),sQuery(id+"F23.wireOp",EDGE,"E161.0"),sQuery(id+"F23.wireOp",EDGE,"E162.0"),sQuery(id+"F23.wireOp",EDGE,"E163.0"),sQuery(id+"F23.wireOp",EDGE,"E164.0"),sQuery(id+"F23.wireOp",EDGE,"E165.0"),sQuery(id+"F23.wireOp",EDGE,"E166.0"),sQuery(id+"F23.wireOp",EDGE,"E167.0"),sQuery(id+"F23.wireOp",EDGE,"E168.0"),sQuery(id+"F23.wireOp",EDGE,"E169.0"),sQuery(id+"F23.wireOp",EDGE,"E170"),sQuery(id+"F23.wireOp",EDGE,"E171"),sQuery(id+"F23.wireOp",EDGE,"E172"),sQuery(id+"F23.wireOp",EDGE,"E173"),sQuery(id+"F23.wireOp",EDGE,"E175.MirrorCS"),sQuery(id+"F23.wireOp",EDGE,"E176.MirrorCS"),sQuery(id+"F23.wireOp",EDGE,"E177.MirrorCS"),sQuery(id+"F23.wireOp",EDGE,"E178.MirrorCS"),sQuery(id+"F23.wireOp",EDGE,"E179.MirrorCS"),sQuery(id+"F23.wireOp",EDGE,"E180.MirrorCS"),sQuery(id+"F23.wireOp",EDGE,"E181.MirrorCS"),sQuery(id+"F23.wireOp",EDGE,"E182.MirrorCS"),sQuery(id+"F23.wireOp",EDGE,"E183.MirrorCS"),sQuery(id+"F23.wireOp",EDGE,"E184.MirrorCS"),sQuery(id+"F23.wireOp",EDGE,"E185.MirrorCS"),sQuery(id+"F23.wireOp",EDGE,"E186.MirrorCS"),sQuery(id+"F23.wireOp",EDGE,"E187.MirrorCS"),sQuery(id+"F23.wireOp",EDGE,"E188.MirrorCS"),sQuery(id+"F23.wireOp",EDGE,"E189"),sQuery(id+"F23.wireOp",EDGE,"E190"),sQuery(id+"F23.wireOp",EDGE,"E191"),sQuery(id+"F23.wireOp",EDGE,"E192.MirrorCS"),sQuery(id+"F23.wireOp",EDGE,"E193.MirrorCS"),sQuery(id+"F23.wireOp",EDGE,"E194.MirrorCS")])],"isStart":true});
            var sketch = newSketch(context, id + "F27", { "sketchPlane" : qUnion([Q0])});
            skLineSegment(sketch, "E207.bottom", {"start": v(25.4, -107.3) * mm, "end": v(-25.4, -107.3) * mm});
            skLineSegment(sketch, "E207.top", {"start": v(25.4, -166.5) * mm, "end": v(-25.4, -166.5) * mm});
            skLineSegment(sketch, "E207.left", {"start": v(25.4, -107.3) * mm, "end": v(25.4, -166.5) * mm});
            skLineSegment(sketch, "E207.right", {"start": v(-25.4, -107.3) * mm, "end": v(-25.4, -166.5) * mm});
            skPoint(sketch, "E207.middle", {"position": v(0, -136.9) * mm});
            skPoint(sketch, "E207.middle.positionSnap0", {"position": v(0, -143.9) * mm});
            skPoint(sketch, "E207.centerSnap0", {"position": v(0, -143.9) * mm});
            skLineSegment(sketch, "E208.bottom", {"start": v(-9.5, -115.06) * mm, "end": v(-17.88, -115.06) * mm});
            skLineSegment(sketch, "E208.top", {"start": v(-9.5, -158.75) * mm, "end": v(-17.88, -158.75) * mm});
            skLineSegment(sketch, "E208.left", {"start": v(-9.5, -115.06) * mm, "end": v(-9.5, -158.75) * mm});
            skLineSegment(sketch, "E208.right", {"start": v(-17.88, -115.06) * mm, "end": v(-17.88, -158.75) * mm});
            skPoint(sketch, "E208.middle", {"position": v(-13.69, -136.9) * mm});
            skLineSegment(sketch, "E209", {"start": v(0, -107.3) * mm, "end": v(0, -166.5) * mm, "construction": true});
            skLineSegment(sketch, "E210.MirrorCS", {"start": v(9.5, -115.06) * mm, "end": v(9.5, -158.75) * mm});
            skLineSegment(sketch, "E211.MirrorCS", {"start": v(9.5, -115.06) * mm, "end": v(17.88, -115.06) * mm});
            skLineSegment(sketch, "E212.MirrorCS", {"start": v(17.88, -115.06) * mm, "end": v(17.88, -158.75) * mm});
            skLineSegment(sketch, "E213.MirrorCS", {"start": v(9.5, -158.75) * mm, "end": v(17.88, -158.75) * mm});
            skSolve(sketch);
        }
        {
            var Q0;
            Q0=makeQuery(id+"F27.imprint","IMPRINT",FACE,{"disambiguationData":[TD([[makeQuery(id+"F27.imprint","IMPRINT",EDGE,{"derivedFrom":sQuery(id+"F27.wireOp",EDGE,"E207.bottom")}),1.0]])]});
            var Q1;
            Q1=makeQuery(id+"F27.imprint","IMPRINT",FACE,{"disambiguationData":[TD([[makeQuery(id+"F27.imprint","IMPRINT",EDGE,{"derivedFrom":sQuery(id+"F27.wireOp",EDGE,"E208.bottom")}),1.0]])]});
            var Q2;
            Q2=makeQuery(id+"F27.imprint","IMPRINT",FACE,{"disambiguationData":[TD([[makeQuery(id+"F27.imprint","IMPRINT",EDGE,{"derivedFrom":sQuery(id+"F27.wireOp",EDGE,"E210.MirrorCS")}),1.0]])]});
            extrude(context, id + "F28", {"entities" : qUnion([Q0, Q1, Q2]), "depth" : 6.35 * mm});
        }
        {
            var Q0;
            Q0=makeQuery(id+"F24.opExtrude","CAP_FACE",FACE,{"disambiguationData":[OSD([sQuery(id+"F23.wireOp",EDGE,"E158.0"),sQuery(id+"F23.wireOp",EDGE,"E159.0"),sQuery(id+"F23.wireOp",EDGE,"E160.0"),sQuery(id+"F23.wireOp",EDGE,"E161.0"),sQuery(id+"F23.wireOp",EDGE,"E162.0"),sQuery(id+"F23.wireOp",EDGE,"E163.0"),sQuery(id+"F23.wireOp",EDGE,"E164.0"),sQuery(id+"F23.wireOp",EDGE,"E165.0"),sQuery(id+"F23.wireOp",EDGE,"E166.0"),sQuery(id+"F23.wireOp",EDGE,"E167.0"),sQuery(id+"F23.wireOp",EDGE,"E168.0"),sQuery(id+"F23.wireOp",EDGE,"E169.0"),sQuery(id+"F23.wireOp",EDGE,"E170"),sQuery(id+"F23.wireOp",EDGE,"E171"),sQuery(id+"F23.wireOp",EDGE,"E172"),sQuery(id+"F23.wireOp",EDGE,"E173"),sQuery(id+"F23.wireOp",EDGE,"E175.MirrorCS"),sQuery(id+"F23.wireOp",EDGE,"E176.MirrorCS"),sQuery(id+"F23.wireOp",EDGE,"E177.MirrorCS"),sQuery(id+"F23.wireOp",EDGE,"E178.MirrorCS"),sQuery(id+"F23.wireOp",EDGE,"E179.MirrorCS"),sQuery(id+"F23.wireOp",EDGE,"E180.MirrorCS"),sQuery(id+"F23.wireOp",EDGE,"E181.MirrorCS"),sQuery(id+"F23.wireOp",EDGE,"E182.MirrorCS"),sQuery(id+"F23.wireOp",EDGE,"E183.MirrorCS"),sQuery(id+"F23.wireOp",EDGE,"E184.MirrorCS"),sQuery(id+"F23.wireOp",EDGE,"E185.MirrorCS"),sQuery(id+"F23.wireOp",EDGE,"E186.MirrorCS"),sQuery(id+"F23.wireOp",EDGE,"E187.MirrorCS"),sQuery(id+"F23.wireOp",EDGE,"E188.MirrorCS"),sQuery(id+"F23.wireOp",EDGE,"E189"),sQuery(id+"F23.wireOp",EDGE,"E190"),sQuery(id+"F23.wireOp",EDGE,"E191"),sQuery(id+"F23.wireOp",EDGE,"E192.MirrorCS"),sQuery(id+"F23.wireOp",EDGE,"E193.MirrorCS"),sQuery(id+"F23.wireOp",EDGE,"E194.MirrorCS")])],"isStart":true});
            var sketch = newSketch(context, id + "F29", { "sketchPlane" : qUnion([Q0])});
            skLineSegment(sketch, "E214", {"start": v(0, -143.9) * mm, "end": v(0, -49.15) * mm, "construction": true});
            skCircle(sketch, "E215", {"center": v(0, -87.82) * mm, "radius": 1.27 * mm});
            skCircle(sketch, "E216.0.1.0", {"center": v(0, -100.52) * mm, "radius": 1.27 * mm});
            skCircle(sketch, "E216.0.2.0", {"center": v(0, -113.22) * mm, "radius": 1.27 * mm});
            skCircle(sketch, "E216.0.3.0", {"center": v(0, -125.92) * mm, "radius": 1.27 * mm});
            skCircle(sketch, "E216.0.4.0", {"center": v(0, -138.62) * mm, "radius": 1.27 * mm});
            skCircle(sketch, "E216.0.5.0", {"center": v(0, -151.32) * mm, "radius": 1.27 * mm});
            skCircle(sketch, "E216.0.6.0", {"center": v(0, -164.02) * mm, "radius": 1.27 * mm});
            skCircle(sketch, "E216.1.0.0", {"center": v(12.7, -87.82) * mm, "radius": 1.27 * mm});
            skCircle(sketch, "E216.1.1.0", {"center": v(12.7, -100.52) * mm, "radius": 1.27 * mm});
            skCircle(sketch, "E216.1.2.0", {"center": v(12.7, -113.22) * mm, "radius": 1.27 * mm});
            skCircle(sketch, "E216.1.3.0", {"center": v(12.7, -125.92) * mm, "radius": 1.27 * mm});
            skCircle(sketch, "E216.1.4.0", {"center": v(12.7, -138.62) * mm, "radius": 1.27 * mm});
            skCircle(sketch, "E216.1.5.0", {"center": v(12.7, -151.32) * mm, "radius": 1.27 * mm});
            skCircle(sketch, "E216.1.6.0", {"center": v(12.7, -164.02) * mm, "radius": 1.27 * mm});
            skCircle(sketch, "E216.2.0.0", {"center": v(25.4, -87.82) * mm, "radius": 1.27 * mm});
            skCircle(sketch, "E216.2.1.0", {"center": v(25.4, -100.52) * mm, "radius": 1.27 * mm});
            skCircle(sketch, "E216.2.2.0", {"center": v(25.4, -113.22) * mm, "radius": 1.27 * mm});
            skCircle(sketch, "E216.2.3.0", {"center": v(25.4, -125.92) * mm, "radius": 1.27 * mm});
            skCircle(sketch, "E216.2.4.0", {"center": v(25.4, -138.62) * mm, "radius": 1.27 * mm});
            skCircle(sketch, "E216.2.5.0", {"center": v(25.4, -151.32) * mm, "radius": 1.27 * mm});
            skCircle(sketch, "E216.2.6.0", {"center": v(25.4, -164.02) * mm, "radius": 1.27 * mm});
            skCircle(sketch, "E216.3.0.0", {"center": v(38.1, -87.82) * mm, "radius": 1.27 * mm});
            skCircle(sketch, "E216.3.1.0", {"center": v(38.1, -100.52) * mm, "radius": 1.27 * mm});
            skCircle(sketch, "E216.3.2.0", {"center": v(38.1, -113.22) * mm, "radius": 1.27 * mm});
            skCircle(sketch, "E216.3.3.0", {"center": v(38.1, -125.92) * mm, "radius": 1.27 * mm});
            skCircle(sketch, "E216.3.4.0", {"center": v(38.1, -138.62) * mm, "radius": 1.27 * mm});
            skCircle(sketch, "E216.3.5.0", {"center": v(38.1, -151.32) * mm, "radius": 1.27 * mm});
            skCircle(sketch, "E216.3.6.0", {"center": v(38.1, -164.02) * mm, "radius": 1.27 * mm});
            skCircle(sketch, "E216.4.0.0", {"center": v(50.8, -87.82) * mm, "radius": 1.27 * mm});
            skCircle(sketch, "E216.4.1.0", {"center": v(50.8, -100.52) * mm, "radius": 1.27 * mm});
            skCircle(sketch, "E216.4.2.0", {"center": v(50.8, -113.22) * mm, "radius": 1.27 * mm});
            skCircle(sketch, "E216.4.3.0", {"center": v(50.8, -125.92) * mm, "radius": 1.27 * mm});
            skCircle(sketch, "E216.4.4.0", {"center": v(50.8, -138.62) * mm, "radius": 1.27 * mm});
            skCircle(sketch, "E216.4.5.0", {"center": v(50.8, -151.32) * mm, "radius": 1.27 * mm});
            skCircle(sketch, "E216.4.6.0", {"center": v(50.8, -164.02) * mm, "radius": 1.27 * mm});
            skLineSegment(sketch, "E216.direction1", {"start": v(0, -87.82) * mm, "end": v(12.7, -87.82) * mm, "construction": true});
            skLineSegment(sketch, "E216.direction2", {"start": v(0, -87.82) * mm, "end": v(0, -100.52) * mm, "construction": true});
            skSolve(sketch);
        }
        {
            var Q0;
            Q0=qCreatedBy(makeId("Front.planeOp"),FACE);
            var sketch = newSketch(context, id + "F30", { "sketchPlane" : qUnion([Q0])});
            skCircle(sketch, "E217.0", {"center": v(0, 0) * mm, "radius": 63.5 * mm});
            skArc(sketch, "E218.MirrorC", {"start": v(120.86, 50.8) * mm, "mid": v(146.22, 43.9) * mm, "end": v(164.74, 25.24) * mm, "construction": true});
            skLineSegment(sketch, "E219.bottom", {"start": v(-66.05, 32.91) * mm, "end": v(-77.49, 38.42) * mm});
            skLineSegment(sketch, "E219.top", {"start": v(-60.54, 44.36) * mm, "end": v(-123.48, 74.65) * mm});
            skLineSegment(sketch, "E219.left", {"start": v(-60.54, 44.36) * mm, "end": v(-66.05, 32.91) * mm});
            skLineSegment(sketch, "E219.right", {"start": v(-123.48, 74.65) * mm, "end": v(-128.98, 63.2) * mm});
            skLineSegment(sketch, "E220", {"start": v(-120.65, 0) * mm, "end": v(-97.52, 48.06) * mm, "construction": true});
            skLineSegment(sketch, "E221.trimOffspring", {"start": v(-117.54, 57.7) * mm, "end": v(-128.98, 63.2) * mm});
            skLineSegment(sketch, "E222", {"start": v(-117.54, 57.7) * mm, "end": v(-97.52, 48.06) * mm, "construction": true});
            skLineSegment(sketch, "E223", {"start": v(-97.52, 48.06) * mm, "end": v(-77.49, 38.42) * mm, "construction": true});
            skArc(sketch, "E224", {"start": v(-120.86, 50.8) * mm, "mid": v(-146.22, 43.9) * mm, "end": v(-164.74, 25.24) * mm, "construction": true});
            skArc(sketch, "E225", {"start": v(-80.81, 31.52) * mm, "mid": v(-98.62, 45.77) * mm, "end": v(-120.86, 50.8) * mm, "construction": true});
            skLineSegment(sketch, "E226.MirrorCS", {"start": v(60.54, 44.36) * mm, "end": v(123.48, 74.65) * mm});
            skLineSegment(sketch, "E227.MirrorCS", {"start": v(123.48, 74.65) * mm, "end": v(128.98, 63.2) * mm});
            skLineSegment(sketch, "E228.MirrorCS", {"start": v(117.54, 57.7) * mm, "end": v(128.98, 63.2) * mm});
            skLineSegment(sketch, "E229.MirrorCS", {"start": v(117.54, 57.7) * mm, "end": v(97.52, 48.06) * mm, "construction": true});
            skLineSegment(sketch, "E230.MirrorCS", {"start": v(97.52, 48.06) * mm, "end": v(77.49, 38.42) * mm, "construction": true});
            skLineSegment(sketch, "E231.MirrorCS", {"start": v(66.05, 32.91) * mm, "end": v(77.49, 38.42) * mm});
            skLineSegment(sketch, "E232.MirrorCS", {"start": v(60.54, 44.36) * mm, "end": v(66.05, 32.91) * mm});
            skPoint(sketch, "E233.MirrorCS.end.orphan", {"position": v(120.86, 50.8) * mm});
            skPoint(sketch, "E233.MirrorCS.start.orphan", {"position": v(80.81, 31.52) * mm});
            skArc(sketch, "E234.MirrorCS", {"start": v(80.81, 31.52) * mm, "mid": v(98.62, 45.77) * mm, "end": v(120.86, 50.8) * mm, "construction": true});
            skCircle(sketch, "E235", {"center": v(0, 0) * mm, "radius": 240 * mm, "construction": true});
            skPoint(sketch, "E236.middle", {"position": v(0, 151.13) * mm});
            skPoint(sketch, "E237.middle", {"position": v(0, -139.7) * mm});
            skLineSegment(sketch, "E238", {"start": v(-9.53, 151.13) * mm, "end": v(9.53, 151.13) * mm, "construction": true});
            skLineSegment(sketch, "E239", {"start": v(0, 141.6) * mm, "end": v(0, 160.66) * mm, "construction": true});
            skLineSegment(sketch, "E240", {"start": v(-9.53, -139.7) * mm, "end": v(9.53, -139.7) * mm, "construction": true});
            skLineSegment(sketch, "E241", {"start": v(0, -130.18) * mm, "end": v(0, -149.23) * mm, "construction": true});
            skCircle(sketch, "E242", {"center": v(-9.53, -139.7) * mm, "radius": 3.18 * mm});
            skCircle(sketch, "E243", {"center": v(0, -149.23) * mm, "radius": 3.18 * mm});
            skCircle(sketch, "E244.MirrorC", {"center": v(9.53, -139.7) * mm, "radius": 3.18 * mm});
            skCircle(sketch, "E245.MirrorC", {"center": v(0, -130.18) * mm, "radius": 3.18 * mm});
            skCircle(sketch, "E246", {"center": v(-9.53, 151.13) * mm, "radius": 3.18 * mm});
            skCircle(sketch, "E247", {"center": v(0, 141.6) * mm, "radius": 3.18 * mm});
            skCircle(sketch, "E248.MirrorC", {"center": v(0, 160.66) * mm, "radius": 3.18 * mm});
            skCircle(sketch, "E249.MirrorC", {"center": v(9.53, 151.13) * mm, "radius": 3.18 * mm});
            skLineSegment(sketch, "E250", {"start": v(-25.4, -203.35) * mm, "end": v(-63.5, -203.35) * mm});
            skLineSegment(sketch, "E251.MirrorCS", {"start": v(82.55, 100.05) * mm, "end": v(82.55, 193.18) * mm});
            skLineSegment(sketch, "E252.MirrorCS", {"start": v(76.2, -190.65) * mm, "end": v(76.2, -76.14) * mm});
            skArc(sketch, "E253", {"start": v(77.32, 203.45) * mm, "mid": v(0, 228.6) * mm, "end": v(-77.32, 203.45) * mm});
            skLineSegment(sketch, "E254", {"start": v(25.4, -203.35) * mm, "end": v(63.5, -203.35) * mm});
            skArc(sketch, "E255.0", {"start": v(75.08, 197.21) * mm, "mid": v(0, 222.25) * mm, "end": v(-75.08, 197.21) * mm});
            skLineSegment(sketch, "E256", {"start": v(-76.2, 194.97) * mm, "end": v(-76.2, 172.57) * mm});
            skLineSegment(sketch, "E257", {"start": v(-73.4, 169.76) * mm, "end": v(73.4, 169.76) * mm});
            skLineSegment(sketch, "E258", {"start": v(76.2, 172.57) * mm, "end": v(76.2, 194.97) * mm});
            skLineSegment(sketch, "E259.bottom", {"start": v(-23, -95.25) * mm, "end": v(23, -95.25) * mm, "construction": true});
            skLineSegment(sketch, "E259.top", {"start": v(-23, -165.25) * mm, "end": v(23, -165.25) * mm, "construction": true});
            skLineSegment(sketch, "E259.left", {"start": v(-23, -95.25) * mm, "end": v(-23, -165.25) * mm, "construction": true});
            skLineSegment(sketch, "E259.right", {"start": v(23, -95.25) * mm, "end": v(23, -165.25) * mm, "construction": true});
            skPoint(sketch, "E259.middle", {"position": v(0, -130.25) * mm});
            skArc(sketch, "E260", {"start": v(-117.54, 57.7) * mm, "mid": v(-146.1, 48.67) * mm, "end": v(-164.74, 25.24) * mm});
            skArc(sketch, "E261", {"start": v(-164.74, 25.24) * mm, "mid": v(-142.68, -45.77) * mm, "end": v(-73.42, -18.71) * mm});
            skArc(sketch, "E262.MirrorCS", {"start": v(-77.49, 38.42) * mm, "mid": v(-66.74, 10.48) * mm, "end": v(-73.42, -18.71) * mm});
            skArc(sketch, "E263", {"start": v(-73.42, -18.71) * mm, "mid": v(-70.4, 7.4) * mm, "end": v(-80.81, 31.52) * mm, "construction": true});
            skArc(sketch, "E264.MirrorCS", {"start": v(77.49, 38.42) * mm, "mid": v(66.74, 10.48) * mm, "end": v(73.42, -18.71) * mm});
            skArc(sketch, "E265.MirrorCS", {"start": v(117.54, 57.7) * mm, "mid": v(146.1, 48.67) * mm, "end": v(164.74, 25.24) * mm});
            skArc(sketch, "E266", {"start": v(164.74, 25.24) * mm, "mid": v(142.68, -45.77) * mm, "end": v(73.42, -18.71) * mm});
            skArc(sketch, "E267", {"start": v(73.42, -18.71) * mm, "mid": v(70.4, 7.4) * mm, "end": v(80.81, 31.52) * mm, "construction": true});
            skCircle(sketch, "E268", {"center": v(23, -95.25) * mm, "radius": 2.25 * mm});
            skCircle(sketch, "E269", {"center": v(-23, -95.25) * mm, "radius": 2.25 * mm});
            skCircle(sketch, "E270", {"center": v(-23, -165.25) * mm, "radius": 2.25 * mm});
            skCircle(sketch, "E271", {"center": v(23, -165.25) * mm, "radius": 2.25 * mm});
            skPoint(sketch, "E272.visualSharp", {"position": v(-76.2, 169.76) * mm});
            skArc(sketch, "E272.filletArc", {"start": v(-76.2, 172.57) * mm, "mid": v(-75.38, 170.58) * mm, "end": v(-73.4, 169.76) * mm});
            skPoint(sketch, "E273.visualSharp", {"position": v(76.2, 169.76) * mm});
            skArc(sketch, "E273.filletArc", {"start": v(73.4, 169.76) * mm, "mid": v(75.38, 170.58) * mm, "end": v(76.2, 172.57) * mm});
            skPoint(sketch, "E274.visualSharp", {"position": v(76.2, 196.36) * mm});
            skArc(sketch, "E274.filletArc", {"start": v(76.2, 194.97) * mm, "mid": v(75.9, 196.22) * mm, "end": v(75.08, 197.21) * mm});
            skPoint(sketch, "E275.visualSharp", {"position": v(-76.2, 196.36) * mm});
            skArc(sketch, "E275.filletArc", {"start": v(-75.08, 197.21) * mm, "mid": v(-75.9, 196.22) * mm, "end": v(-76.2, 194.97) * mm});
            skArc(sketch, "E276", {"start": v(123.48, -63.44) * mm, "mid": v(191.16, 11.96) * mm, "end": v(123.48, 87.35) * mm});
            skLineSegment(sketch, "E277", {"start": v(123.48, 87.35) * mm, "end": v(95.25, 87.35) * mm});
            skLineSegment(sketch, "E278", {"start": v(123.48, -63.44) * mm, "end": v(88.9, -63.44) * mm});
            skPoint(sketch, "E279.visualSharp", {"position": v(76.2, -63.44) * mm});
            skArc(sketch, "E279.filletArc", {"start": v(88.9, -63.44) * mm, "mid": v(79.92, -67.16) * mm, "end": v(76.2, -76.14) * mm});
            skLineSegment(sketch, "E280.MirrorCS", {"start": v(-82.55, 100.05) * mm, "end": v(-82.55, 193.18) * mm});
            skLineSegment(sketch, "E281.MirrorCS", {"start": v(-123.48, 87.35) * mm, "end": v(-95.25, 87.35) * mm});
            skArc(sketch, "E282.MirrorCS", {"start": v(-123.48, -63.44) * mm, "mid": v(-191.16, 11.96) * mm, "end": v(-123.48, 87.35) * mm});
            skLineSegment(sketch, "E283.MirrorCS", {"start": v(-123.48, -63.44) * mm, "end": v(-88.9, -63.44) * mm});
            skArc(sketch, "E284.MirrorCS", {"start": v(-88.9, -63.44) * mm, "mid": v(-79.92, -67.16) * mm, "end": v(-76.2, -76.14) * mm});
            skLineSegment(sketch, "E285.MirrorCS", {"start": v(-76.2, -190.65) * mm, "end": v(-76.2, -76.14) * mm});
            skLineSegment(sketch, "E286.bottom", {"start": v(35.7, -190.65) * mm, "end": v(63.5, -190.65) * mm});
            skLineSegment(sketch, "E286.top", {"start": v(35.7, -74.1) * mm, "end": v(63.5, -74.1) * mm});
            skLineSegment(sketch, "E286.left", {"start": v(35.7, -190.65) * mm, "end": v(35.7, -74.1) * mm});
            skLineSegment(sketch, "E286.right", {"start": v(63.5, -190.65) * mm, "end": v(63.5, -74.1) * mm});
            skLineSegment(sketch, "E287.MirrorCS", {"start": v(-35.7, -74.1) * mm, "end": v(-63.5, -74.1) * mm});
            skLineSegment(sketch, "E288.MirrorCS", {"start": v(-63.5, -190.65) * mm, "end": v(-63.5, -74.1) * mm});
            skLineSegment(sketch, "E289.MirrorCS", {"start": v(-35.7, -190.65) * mm, "end": v(-35.7, -74.1) * mm});
            skLineSegment(sketch, "E290.MirrorCS", {"start": v(-35.7, -190.65) * mm, "end": v(-63.5, -190.65) * mm});
            skLineSegment(sketch, "E291.top", {"start": v(-23, -88.92) * mm, "end": v(23, -88.92) * mm});
            skLineSegment(sketch, "E291.left", {"start": v(-23, -59.19) * mm, "end": v(-23, -88.92) * mm});
            skLineSegment(sketch, "E291.right", {"start": v(23, -59.19) * mm, "end": v(23, -88.92) * mm});
            skLineSegment(sketch, "E292", {"start": v(0, 0) * mm, "end": v(0, 192.19) * mm, "construction": true});
            skPoint(sketch, "E292.endSnap0", {"position": v(0, 176.14) * mm});
            skPoint(sketch, "E293", {"position": v(0, 169.76) * mm});
            skLineSegment(sketch, "E294.bottom", {"start": v(76.2, 159.6) * mm, "end": v(19.05, 159.6) * mm});
            skLineSegment(sketch, "E294.top", {"start": v(76.2, 68.34) * mm, "end": v(19.05, 68.34) * mm});
            skLineSegment(sketch, "E294.left", {"start": v(76.2, 159.6) * mm, "end": v(76.2, 68.34) * mm});
            skLineSegment(sketch, "E294.right", {"start": v(19.05, 159.6) * mm, "end": v(19.05, 68.34) * mm});
            skLineSegment(sketch, "E295.MirrorCS", {"start": v(-19.05, 159.6) * mm, "end": v(-19.05, 68.34) * mm});
            skLineSegment(sketch, "E296.MirrorCS", {"start": v(-76.2, 159.6) * mm, "end": v(-19.05, 159.6) * mm});
            skLineSegment(sketch, "E297.MirrorCS", {"start": v(-76.2, 159.6) * mm, "end": v(-76.2, 68.34) * mm});
            skLineSegment(sketch, "E298.MirrorCS", {"start": v(-76.2, 68.34) * mm, "end": v(-19.05, 68.34) * mm});
            skPoint(sketch, "E299.visualSharp", {"position": v(-76.2, -203.35) * mm});
            skArc(sketch, "E299.filletArc", {"start": v(-76.2, -190.65) * mm, "mid": v(-72.48, -199.63) * mm, "end": v(-63.5, -203.35) * mm});
            skPoint(sketch, "E300.visualSharp", {"position": v(76.2, -203.35) * mm});
            skArc(sketch, "E300.filletArc", {"start": v(63.5, -203.35) * mm, "mid": v(72.48, -199.63) * mm, "end": v(76.2, -190.65) * mm});
            skLineSegment(sketch, "E301.top", {"start": v(25.4, -190.65) * mm, "end": v(-25.4, -190.65) * mm});
            skLineSegment(sketch, "E301.left", {"start": v(25.4, -203.35) * mm, "end": v(25.4, -190.65) * mm});
            skLineSegment(sketch, "E301.right", {"start": v(-25.4, -203.35) * mm, "end": v(-25.4, -190.65) * mm});
            skPoint(sketch, "E301.middle", {"position": v(0, -197) * mm});
            skPoint(sketch, "E302.orphan", {"position": v(0, -203.35) * mm});
            skPoint(sketch, "E303.visualSharp", {"position": v(82.55, 87.35) * mm});
            skArc(sketch, "E303.filletArc", {"start": v(82.55, 100.05) * mm, "mid": v(86.27, 91.07) * mm, "end": v(95.25, 87.35) * mm});
            skPoint(sketch, "E304.visualSharp", {"position": v(-82.55, 87.35) * mm});
            skArc(sketch, "E304.filletArc", {"start": v(-95.25, 87.35) * mm, "mid": v(-86.27, 91.07) * mm, "end": v(-82.55, 100.05) * mm});
            skPoint(sketch, "E305.visualSharp", {"position": v(-82.55, 199.44) * mm});
            skArc(sketch, "E305.filletArc", {"start": v(-77.32, 203.45) * mm, "mid": v(-81.17, 198.94) * mm, "end": v(-82.55, 193.18) * mm});
            skPoint(sketch, "E306.visualSharp", {"position": v(82.55, 199.44) * mm});
            skArc(sketch, "E306.filletArc", {"start": v(82.55, 193.18) * mm, "mid": v(81.17, 198.94) * mm, "end": v(77.32, 203.45) * mm});
            skSolve(sketch);
        }
        {
            var Q0;
            Q0=makeQuery(id+"F30.imprint","IMPRINT",FACE,{"disambiguationData":[TD([[makeQuery(id+"F30.imprint","IMPRINT",EDGE,{"derivedFrom":sQuery(id+"F30.wireOp",EDGE,"E219.bottom")}),1.0]])]});
            extrude(context, id + "F31", {"entities" : qUnion([Q0]), "depth" : 12.7 * mm});
        }
    });
